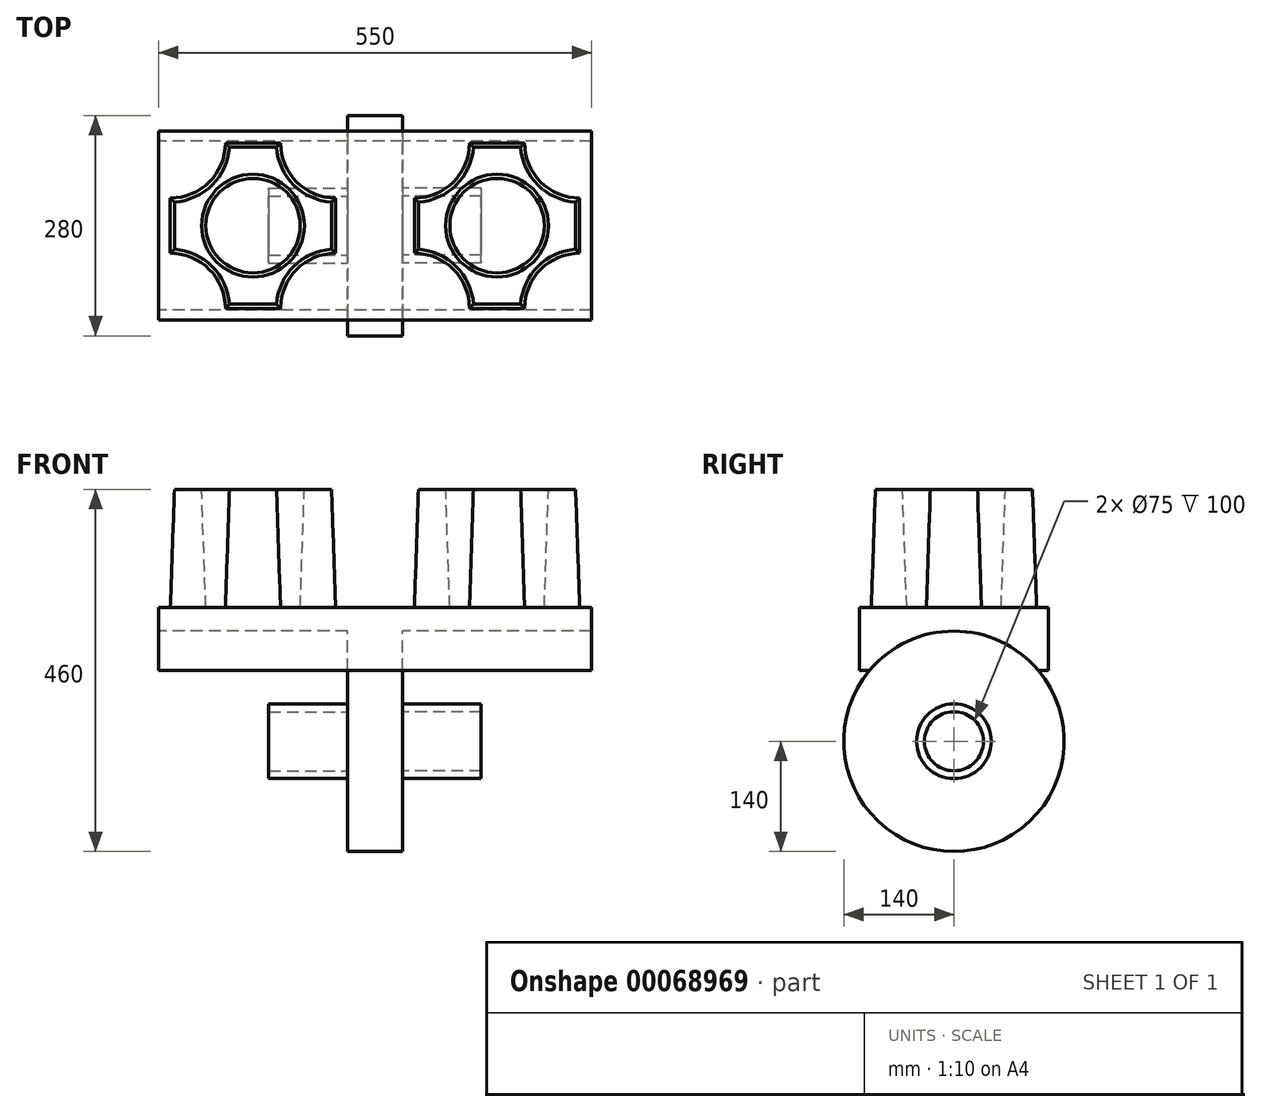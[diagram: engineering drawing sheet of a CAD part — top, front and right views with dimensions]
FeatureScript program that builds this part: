
annotation { "Feature Type Name" : "Feature", "Feature Type Description" : "" }
export const myFeature = defineFeature(function(context is Context, id is Id, definition is map)
    precondition{}
    {
        {
            var Q0;
            Q0=qCreatedBy(makeId("Top.planeOp"),FACE);
            var sketch = newSketch(context, id + "F0", { "sketchPlane" : qUnion([Q0])});
            skLineSegment(sketch, "E0.rect.bottom", {"start": v(275, -120) * mm, "end": v(-275, -120) * mm});
            skLineSegment(sketch, "E0.rect.top", {"start": v(275, 120) * mm, "end": v(-275, 120) * mm});
            skLineSegment(sketch, "E0.rect.left", {"start": v(275, -120) * mm, "end": v(275, 120) * mm});
            skLineSegment(sketch, "E0.rect.right", {"start": v(-275, -120) * mm, "end": v(-275, 120) * mm});
            skPoint(sketch, "E0.rect.middle", {"position": v(0, 0) * mm});
            skSolve(sketch);
        }
        {
            var Q0;
            Q0=makeQuery(id+"F0.imprint","IMPRINT",FACE,{"disambiguationData":[TD([[makeQuery(id+"F0.imprint","IMPRINT",EDGE,{"derivedFrom":sQuery(id+"F0.wireOp",EDGE,"E0.rect.bottom")}),-1.0]])]});
            extrude(context, id + "F1", {"entities" : qUnion([Q0]), "depth" : 80 * mm});
        }
        {
            var Q0;
            Q0=makeQuery(id+"F1.opExtrude","SWEPT_FACE",FACE,{"disambiguationData":[OSD([sQuery(id+"F0.wireOp",EDGE,"E0.rect.right")])]});
            var sketch = newSketch(context, id + "F2", { "sketchPlane" : qUnion([Q0])});
            skCircle(sketch, "E1", {"center": v(0, -90) * mm, "radius": 140 * mm});
            skSolve(sketch);
        }
        {
            var Q0;
            {var subQ0=sQuery(id+"F2.wireOp",EDGE,"E1");var subQ1=makeQuery(id+"F1.opExtrude","CAP_EDGE",EDGE,{"disambiguationData":[OSD([sQuery(id+"F0.wireOp",EDGE,"E0.rect.right")])],"isStart":true});var subQ2=makeQuery(id+"F2.imprint","INTERSECT",VERTEX,{"disambiguationData":[OD(0.0)],"derivedFrom":[subQ1,subQ0]});Q0=makeQuery(id+"F2.imprint","IMPRINT",FACE,{"disambiguationData":[TD([[makeQuery(id+"F2.imprint","IMPRINT",EDGE,{"disambiguationData":[TD([[subQ2,1.0]])],"derivedFrom":subQ0}),1.0]])]});}
            var Q1;
            {var subQ0=sQuery(id+"F2.wireOp",EDGE,"E1");var subQ1=makeQuery(id+"F1.opExtrude","CAP_EDGE",EDGE,{"disambiguationData":[OSD([sQuery(id+"F0.wireOp",EDGE,"E0.rect.right")])],"isStart":true});var subQ2=makeQuery(id+"F2.imprint","INTERSECT",VERTEX,{"disambiguationData":[OD(0.0)],"derivedFrom":[subQ1,subQ0]});Q1=makeQuery(id+"F2.imprint","IMPRINT",FACE,{"disambiguationData":[TD([[makeQuery(id+"F2.imprint","IMPRINT",EDGE,{"disambiguationData":[TD([[subQ2,-1.0]])],"derivedFrom":subQ0}),1.0]])]});}
            extrude(context, id + "F3", {"entities" : qUnion([Q0, Q1]), "operationType" : NewBodyOperationType.REMOVE, "oppositeDirection" : true, "depth" : 656.55 * mm});
        }
        {
            var Q0;
            Q0=qCreatedBy(makeId("Right.planeOp"),FACE);
            var sketch = newSketch(context, id + "F4", { "sketchPlane" : qUnion([Q0])});
            skCircle(sketch, "E2", {"center": v(0, -90) * mm, "radius": 140 * mm});
            skSolve(sketch);
        }
        {
            var Q0;
            Q0=makeQuery(id+"F4.imprint","IMPRINT",FACE,{"disambiguationData":[TD([[makeQuery(id+"F4.imprint","IMPRINT",EDGE,{"derivedFrom":sQuery(id+"F4.wireOp",EDGE,"E2")}),1.0]])]});
            extrude(context, id + "F5", {"entities" : qUnion([Q0]), "operationType" : NewBodyOperationType.ADD, "depth" : 35 * mm, "hasSecondDirection" : true, "secondDirectionOppositeDirection" : true, "secondDirectionDepth" : 35 * mm});
        }
        {
            var Q0;
            Q0=makeQuery(id+"F5.opExtrude","CAP_FACE",FACE,{"disambiguationData":[OSD([sQuery(id+"F4.wireOp",EDGE,"E2")])],"isStart":false});
            var sketch = newSketch(context, id + "F6", { "sketchPlane" : qUnion([Q0])});
            skCircle(sketch, "E3", {"center": v(0, -90) * mm, "radius": 37.5 * mm});
            skCircle(sketch, "E4", {"center": v(0, -90) * mm, "radius": 47.5 * mm});
            skSolve(sketch);
        }
        {
            var Q0;
            Q0=makeQuery(id+"F6.imprint","IMPRINT",FACE,{"disambiguationData":[TD([[makeQuery(id+"F6.imprint","IMPRINT",EDGE,{"derivedFrom":sQuery(id+"F6.wireOp",EDGE,"E3")}),-1.0]])]});
            extrude(context, id + "F7", {"entities" : qUnion([Q0]), "operationType" : NewBodyOperationType.ADD, "depth" : 100 * mm});
        }
        {
            var Q0;
            Q0=makeQuery(id+"F1.opExtrude","SWEPT_BODY",BODY,{"disambiguationData":[OSD([sQuery(id+"F0.wireOp",EDGE,"E0.rect.bottom"),sQuery(id+"F0.wireOp",EDGE,"E0.rect.top"),sQuery(id+"F0.wireOp",EDGE,"E0.rect.left"),sQuery(id+"F0.wireOp",EDGE,"E0.rect.right")])]});
            var Q1;
            Q1=qCreatedBy(makeId("Right.planeOp"),FACE);
            mirror(context, id + "F8", {"operationType" : NewBodyOperationType.ADD, "entities" : qUnion([Q0]), "mirrorPlane" : qUnion([Q1])});
        }
        {
            var Q0;
            Q0=makeQuery(id+"F1.opExtrude","CAP_FACE",FACE,{"disambiguationData":[OSD([sQuery(id+"F0.wireOp",EDGE,"E0.rect.bottom"),sQuery(id+"F0.wireOp",EDGE,"E0.rect.top"),sQuery(id+"F0.wireOp",EDGE,"E0.rect.left"),sQuery(id+"F0.wireOp",EDGE,"E0.rect.right")])],"isStart":false});
            var sketch = newSketch(context, id + "F9", { "sketchPlane" : qUnion([Q0])});
            skLineSegment(sketch, "E5.rect.bottom", {"start": v(-120, -105) * mm, "end": v(-190, -105) * mm});
            skLineSegment(sketch, "E5.rect.top", {"start": v(-120, 105) * mm, "end": v(-190, 105) * mm});
            skLineSegment(sketch, "E5.rect.left", {"start": v(-50, -35) * mm, "end": v(-50, 35) * mm});
            skLineSegment(sketch, "E5.rect.right", {"start": v(-260, -35) * mm, "end": v(-260, 35) * mm});
            skPoint(sketch, "E5.rect.middle", {"position": v(-155, 0) * mm});
            skArc(sketch, "E6", {"start": v(-260, 35) * mm, "mid": v(-210.5, 55.5) * mm, "end": v(-190, 105) * mm});
            skArc(sketch, "E7", {"start": v(-120, 105) * mm, "mid": v(-99.5, 55.5) * mm, "end": v(-50, 35) * mm});
            skArc(sketch, "E8", {"start": v(-190, -105) * mm, "mid": v(-210.5, -55.5) * mm, "end": v(-260, -35) * mm});
            skArc(sketch, "E9", {"start": v(-50, -35) * mm, "mid": v(-99.5, -55.5) * mm, "end": v(-120, -105) * mm});
            skCircle(sketch, "E10", {"center": v(-155, 0) * mm, "radius": 60 * mm});
            skSolve(sketch);
        }
        {
            var Q0;
            Q0 = qSketchRegion(id + "F9", true);
            extrude(context, id + "F10", {"entities" : qUnion([Q0]), "operationType" : NewBodyOperationType.ADD, "depth" : 150 * mm, "hasDraft" : true, "draftAngle" : 2 * degree, "draftPullDirection" : true});
        }
        {
            var Q0;
            Q0=makeQuery(id+"F1.opExtrude","SWEPT_BODY",BODY,{"disambiguationData":[OSD([sQuery(id+"F0.wireOp",EDGE,"E0.rect.bottom"),sQuery(id+"F0.wireOp",EDGE,"E0.rect.top"),sQuery(id+"F0.wireOp",EDGE,"E0.rect.left"),sQuery(id+"F0.wireOp",EDGE,"E0.rect.right")])]});
            var Q1;
            Q1=qCreatedBy(makeId("Right.planeOp"),FACE);
            mirror(context, id + "F11", {"operationType" : NewBodyOperationType.ADD, "entities" : qUnion([Q0]), "mirrorPlane" : qUnion([Q1])});
        }
    });
